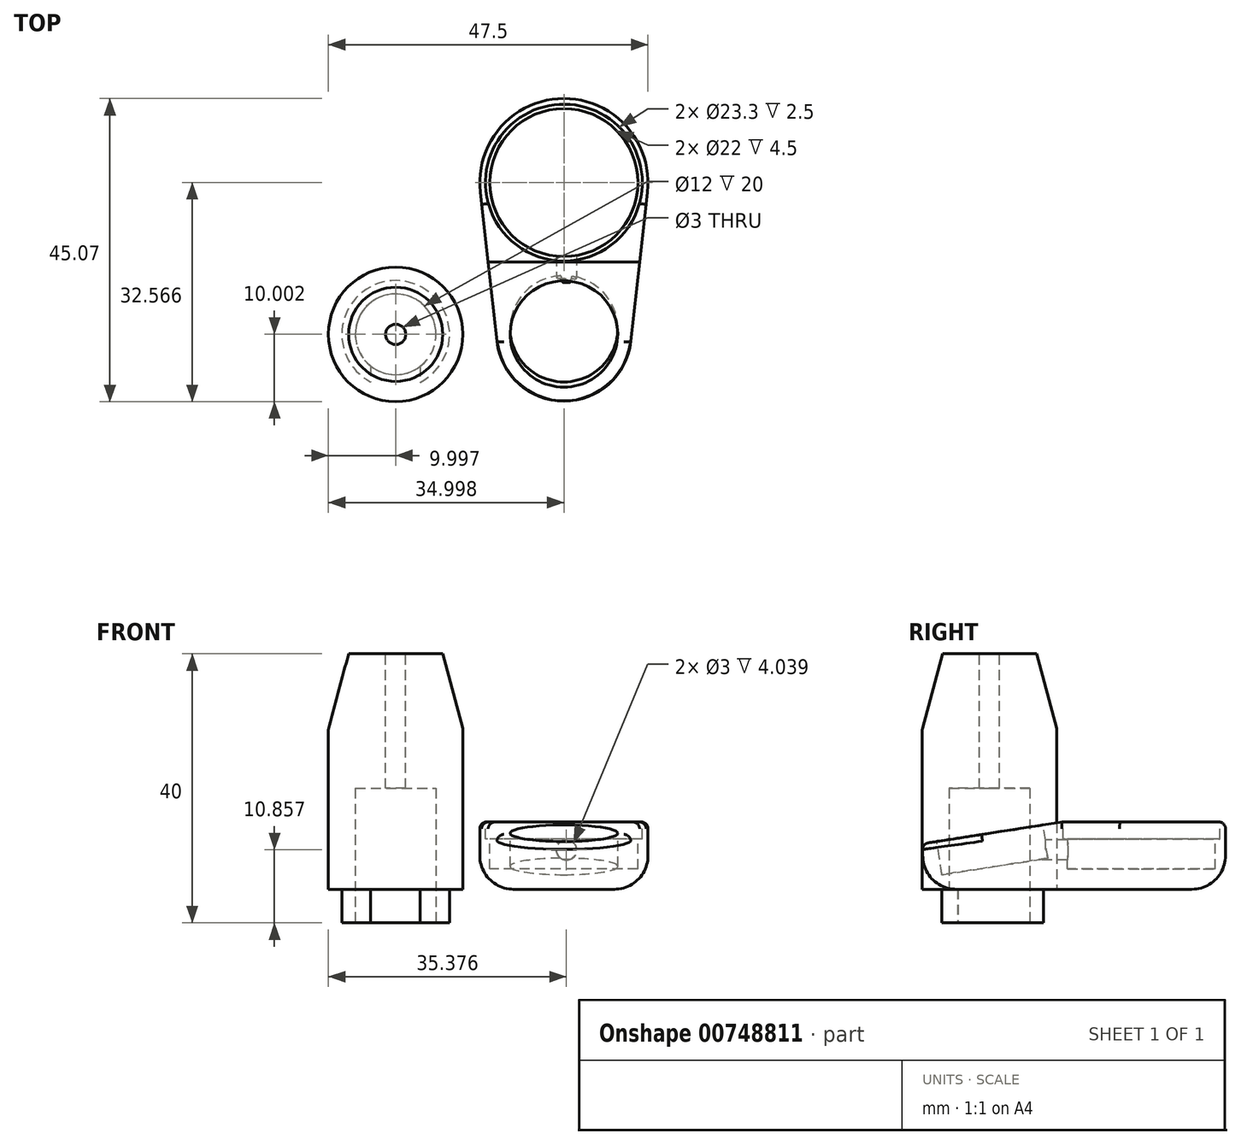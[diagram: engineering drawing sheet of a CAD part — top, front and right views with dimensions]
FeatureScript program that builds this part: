
annotation { "Feature Type Name" : "Feature", "Feature Type Description" : "" }
export const myFeature = defineFeature(function(context is Context, id is Id, definition is map)
    precondition{}
    {
        {
            var Q0;
            Q0=qCreatedBy(makeId("Top.planeOp"),FACE);
            var sketch = newSketch(context, id + "F0", { "sketchPlane" : qUnion([Q0])});
            skCircle(sketch, "E0", {"center": v(-37.82, 33.41) * mm, "radius": 10 * mm});
            skSolve(sketch);
        }
        {
            var Q0;
            Q0 = qSketchRegion(id + "F0", true);
            extrude(context, id + "F1", {"entities" : qUnion([Q0]), "depth" : 35 * mm, "offsetDistance" : 25 * mm});
        }
        {
            var Q0;
            Q0=makeQuery(id+"F1.opExtrude","CAP_EDGE",EDGE,{"disambiguationData":[OSD([sQuery(id+"F0.wireOp",EDGE,"E0")])],"isStart":false});
            chamfer(context, id + "F2", {"entities" : qUnion([Q0]), "chamferType" : ChamferType.OFFSET_ANGLE, "width" : 3 * mm, "oppositeDirection" : false, "angle" : 75 * degree, "tangentPropagation" : true});
        }
        {
            var Q0;
            Q0=makeQuery(id+"F1.opExtrude","CAP_FACE",FACE,{"disambiguationData":[OSD([sQuery(id+"F0.wireOp",EDGE,"E0")])],"isStart":true});
            var sketch = newSketch(context, id + "F3", { "sketchPlane" : qUnion([Q0])});
            skCircle(sketch, "E1", {"center": v(-37.82, -33.41) * mm, "radius": 6 * mm});
            skSolve(sketch);
        }
        {
            var Q0;
            Q0 = qSketchRegion(id + "F3", true);
            extrude(context, id + "F4", {"entities" : qUnion([Q0]), "operationType" : NewBodyOperationType.REMOVE, "oppositeDirection" : true, "depth" : 15 * mm, "offsetDistance" : 25 * mm});
        }
        {
            var Q0;
            Q0=makeQuery(id+"F1.opExtrude","CAP_FACE",FACE,{"disambiguationData":[OSD([sQuery(id+"F0.wireOp",EDGE,"E0")])],"isStart":false});
            var sketch = newSketch(context, id + "F5", { "sketchPlane" : qUnion([Q0])});
            skCircle(sketch, "E2", {"center": v(-37.82, 33.41) * mm, "radius": 1.5 * mm});
            skSolve(sketch);
        }
        {
            var Q0;
            Q0 = qSketchRegion(id + "F5", true);
            extrude(context, id + "F6", {"entities" : qUnion([Q0]), "operationType" : NewBodyOperationType.REMOVE, "oppositeDirection" : true, "depth" : 20 * mm, "offsetDistance" : 25 * mm});
        }
        {
            var Q0;
            Q0=qCreatedBy(makeId("Top.planeOp"),FACE);
            var sketch = newSketch(context, id + "F7", { "sketchPlane" : qUnion([Q0])});
            skCircle(sketch, "E3", {"center": v(-12.82, 33.48) * mm, "radius": 10 * mm});
            skCircle(sketch, "E4", {"center": v(-12.82, 55.98) * mm, "radius": 12.5 * mm});
            skLineSegment(sketch, "E5", {"start": v(-2.88, 32.37) * mm, "end": v(-0.4, 54.59) * mm});
            skLineSegment(sketch, "E6", {"start": v(-22.76, 32.37) * mm, "end": v(-25.25, 54.59) * mm});
            skSolve(sketch);
        }
        {
            var Q0;
            Q0 = qSketchRegion(id + "F7", true);
            extrude(context, id + "F8", {"entities" : qUnion([Q0]), "depth" : 10 * mm, "offsetDistance" : 25 * mm});
        }
        {
            var Q0;
            Q0=qCreatedBy(makeId("Right.planeOp"),FACE);
            var sketch = newSketch(context, id + "F9", { "sketchPlane" : qUnion([Q0])});
            skLineSegment(sketch, "E7", {"start": v(44.3, 10.02) * mm, "end": v(22.05, 6.56) * mm});
            skLineSegment(sketch, "E8", {"start": v(22.05, 6.56) * mm, "end": v(22.05, 10.01) * mm});
            skLineSegment(sketch, "E9", {"start": v(22.05, 10.01) * mm, "end": v(44.3, 10.02) * mm});
            skSolve(sketch);
        }
        {
            var Q0;
            Q0 = qSketchRegion(id + "F9", true);
            extrude(context, id + "F10", {"entities" : qUnion([Q0]), "operationType" : NewBodyOperationType.REMOVE, "oppositeDirection" : true, "depth" : 25 * mm, "offsetDistance" : 25 * mm});
        }
        {
            var Q0;
            Q0=makeQuery(id+"F10.boolean.opBoolean","COPY",FACE,{"derivedFrom":makeQuery(id+"F10.opExtrude","SWEPT_FACE",FACE,{"disambiguationData":[OSD([sQuery(id+"F9.wireOp",EDGE,"E7")])]})});
            var sketch = newSketch(context, id + "F11", { "sketchPlane" : qUnion([Q0])});
            skCircle(sketch, "E10", {"center": v(-12.82, 34.36) * mm, "radius": 8 * mm});
            skSolve(sketch);
        }
        {
            var Q0;
            Q0 = qSketchRegion(id + "F11", true);
            extrude(context, id + "F12", {"entities" : qUnion([Q0]), "operationType" : NewBodyOperationType.REMOVE, "oppositeDirection" : true, "depth" : 5 * mm, "offsetDistance" : 25 * mm});
        }
        {
            var Q0;
            Q0=makeQuery(id+"F1.opExtrude","CAP_FACE",FACE,{"disambiguationData":[OSD([sQuery(id+"F0.wireOp",EDGE,"E0")])],"isStart":true});
            var sketch = newSketch(context, id + "F13", { "sketchPlane" : qUnion([Q0])});
            skCircle(sketch, "E11", {"center": v(-37.82, -33.41) * mm, "radius": 8 * mm});
            skSolve(sketch);
        }
        {
            var Q0;
            Q0 = qSketchRegion(id + "F13", true);
            extrude(context, id + "F14", {"entities" : qUnion([Q0]), "operationType" : NewBodyOperationType.ADD, "depth" : 5 * mm, "offsetDistance" : 25 * mm});
        }
        {
            var Q0;
            Q0=makeQuery(id+"F14.opExtrude","CAP_FACE",FACE,{"disambiguationData":[OSD([sQuery(id+"F13.wireOp",EDGE,"E11")])],"isStart":false});
            var sketch = newSketch(context, id + "F15", { "sketchPlane" : qUnion([Q0])});
            skCircle(sketch, "E12", {"center": v(-37.82, -33.41) * mm, "radius": 6 * mm});
            skSolve(sketch);
        }
        {
            var Q0;
            Q0 = qSketchRegion(id + "F15", true);
            extrude(context, id + "F16", {"entities" : qUnion([Q0]), "operationType" : NewBodyOperationType.REMOVE, "oppositeDirection" : true, "depth" : 5 * mm, "offsetDistance" : 25 * mm});
        }
        {
            var Q0;
            Q0=makeQuery(id+"F14.opExtrude","CAP_FACE",FACE,{"disambiguationData":[OSD([sQuery(id+"F13.wireOp",EDGE,"E11")])],"isStart":false});
            var sketch = newSketch(context, id + "F17", { "sketchPlane" : qUnion([Q0])});
            skLineSegment(sketch, "E13.bottom", {"start": v(-34.18, -29.65) * mm, "end": v(-41.56, -29.65) * mm});
            skLineSegment(sketch, "E13.top", {"start": v(-34.18, -25.18) * mm, "end": v(-41.56, -25.18) * mm});
            skLineSegment(sketch, "E13.left", {"start": v(-34.18, -29.65) * mm, "end": v(-34.18, -25.18) * mm});
            skLineSegment(sketch, "E13.right", {"start": v(-41.56, -29.65) * mm, "end": v(-41.56, -25.18) * mm});
            skPoint(sketch, "E13.middle", {"position": v(-37.87, -27.41) * mm});
            skSolve(sketch);
        }
        {
            var Q0;
            Q0 = qSketchRegion(id + "F17", true);
            extrude(context, id + "F18", {"entities" : qUnion([Q0]), "operationType" : NewBodyOperationType.REMOVE, "oppositeDirection" : true, "depth" : 5 * mm, "offsetDistance" : 25 * mm});
        }
        {
            var Q0;
            Q0=makeQuery(id+"F8.opExtrude","CAP_EDGE",EDGE,{"disambiguationData":[OSD([sQuery(id+"F7.wireOp",EDGE,"E5")])],"isStart":true});
            fillet(context, id + "F19", {"entities" : qUnion([Q0]), "radius" : 5 * mm, "tangentPropagation" : true, "allowEdgeOverflow" : false});
        }
        {
            var Q0;
            Q0=makeQuery(id+"F8.opExtrude","CAP_FACE",FACE,{"disambiguationData":[OSD([sQuery(id+"F7.wireOp",EDGE,"E3"),sQuery(id+"F7.wireOp",EDGE,"E4"),sQuery(id+"F7.wireOp",EDGE,"E5"),sQuery(id+"F7.wireOp",EDGE,"E6")])],"isStart":false});
            var sketch = newSketch(context, id + "F20", { "sketchPlane" : qUnion([Q0])});
            skCircle(sketch, "E14", {"center": v(-12.82, 55.98) * mm, "radius": 11 * mm});
            skSolve(sketch);
        }
        {
            var Q0;
            Q0 = qSketchRegion(id + "F20", true);
            extrude(context, id + "F21", {"entities" : qUnion([Q0]), "operationType" : NewBodyOperationType.REMOVE, "oppositeDirection" : true, "depth" : 7 * mm, "offsetDistance" : 25 * mm});
        }
        {
            var Q0;
            Q0=makeQuery(id+"F8.opExtrude","CAP_FACE",FACE,{"disambiguationData":[OSD([sQuery(id+"F7.wireOp",EDGE,"E3"),sQuery(id+"F7.wireOp",EDGE,"E4"),sQuery(id+"F7.wireOp",EDGE,"E5"),sQuery(id+"F7.wireOp",EDGE,"E6")])],"isStart":false});
            var sketch = newSketch(context, id + "F22", { "sketchPlane" : qUnion([Q0])});
            skCircle(sketch, "E15", {"center": v(-12.82, 55.98) * mm, "radius": 11.65 * mm});
            skSolve(sketch);
        }
        {
            var Q0;
            Q0 = qSketchRegion(id + "F22", true);
            extrude(context, id + "F23", {"entities" : qUnion([Q0]), "operationType" : NewBodyOperationType.REMOVE, "oppositeDirection" : true, "depth" : 2.5 * mm, "offsetDistance" : 25 * mm});
        }
        {
            var Q0;
            Q0=qCreatedBy(makeId("Front.planeOp"),FACE);
            var sketch = newSketch(context, id + "F24", { "sketchPlane" : qUnion([Q0])});
            skCircle(sketch, "E16", {"center": v(-12.44, 5.86) * mm, "radius": 1.5 * mm});
            skSolve(sketch);
        }
        {
            var Q0;
            Q0 = qSketchRegion(id + "F24", true);
            extrude(context, id + "F25", {"entities" : qUnion([Q0]), "operationType" : NewBodyOperationType.REMOVE, "oppositeDirection" : true, "depth" : 55 * mm, "offsetDistance" : 25 * mm, "hasSecondDirection" : true, "secondDirectionOppositeDirection" : true, "secondDirectionDepth" : 41.1 * mm});
        }
        {
            var Q0;
            Q0=makeQuery(id+"F8.opExtrude","CAP_EDGE",EDGE,{"disambiguationData":[OSD([sQuery(id+"F7.wireOp",EDGE,"E6")])],"isStart":false});
            var Q1;
            Q1=makeQuery(id+"F10.boolean.opBoolean","INTERSECT",EDGE,{"derivedFrom":[makeQuery(id+"F8.opExtrude","SWEPT_FACE",FACE,{"disambiguationData":[OSD([sQuery(id+"F7.wireOp",EDGE,"E3")])]}),makeQuery(id+"F10.opExtrude","SWEPT_FACE",FACE,{"disambiguationData":[OSD([sQuery(id+"F9.wireOp",EDGE,"E7")])]})]});
            var Q2;
            Q2=makeQuery(id+"F10.boolean.opBoolean","INTERSECT",EDGE,{"derivedFrom":[makeQuery(id+"F8.opExtrude","SWEPT_FACE",FACE,{"disambiguationData":[OSD([sQuery(id+"F7.wireOp",EDGE,"E5")])]}),makeQuery(id+"F10.opExtrude","SWEPT_FACE",FACE,{"disambiguationData":[OSD([sQuery(id+"F9.wireOp",EDGE,"E7")])]})]});
            var Q3;
            {var subQ0=sQuery(id+"F0.wireOp",EDGE,"E0");Q3=makeQuery(id+"F2.opChamfer","BLEND_EDGE",EDGE,{"blendedFrom":[makeQuery(id+"F1.opExtrude","CAP_EDGE",EDGE,{"disambiguationData":[OSD([subQ0])],"isStart":false}),makeQuery(id+"F1.opExtrude","SWEPT_FACE",FACE,{"disambiguationData":[OSD([subQ0])]})],"blendedInto":[makeQuery(id+"F1.opExtrude","SWEPT_FACE",FACE,{"disambiguationData":[OSD([subQ0])]})]});}
            fillet(context, id + "F26", {"entities" : qUnion([Q0, Q1, Q2, Q3]), "radius" : 1 * mm, "tangentPropagation" : true, "allowEdgeOverflow" : false});
        }
    });
